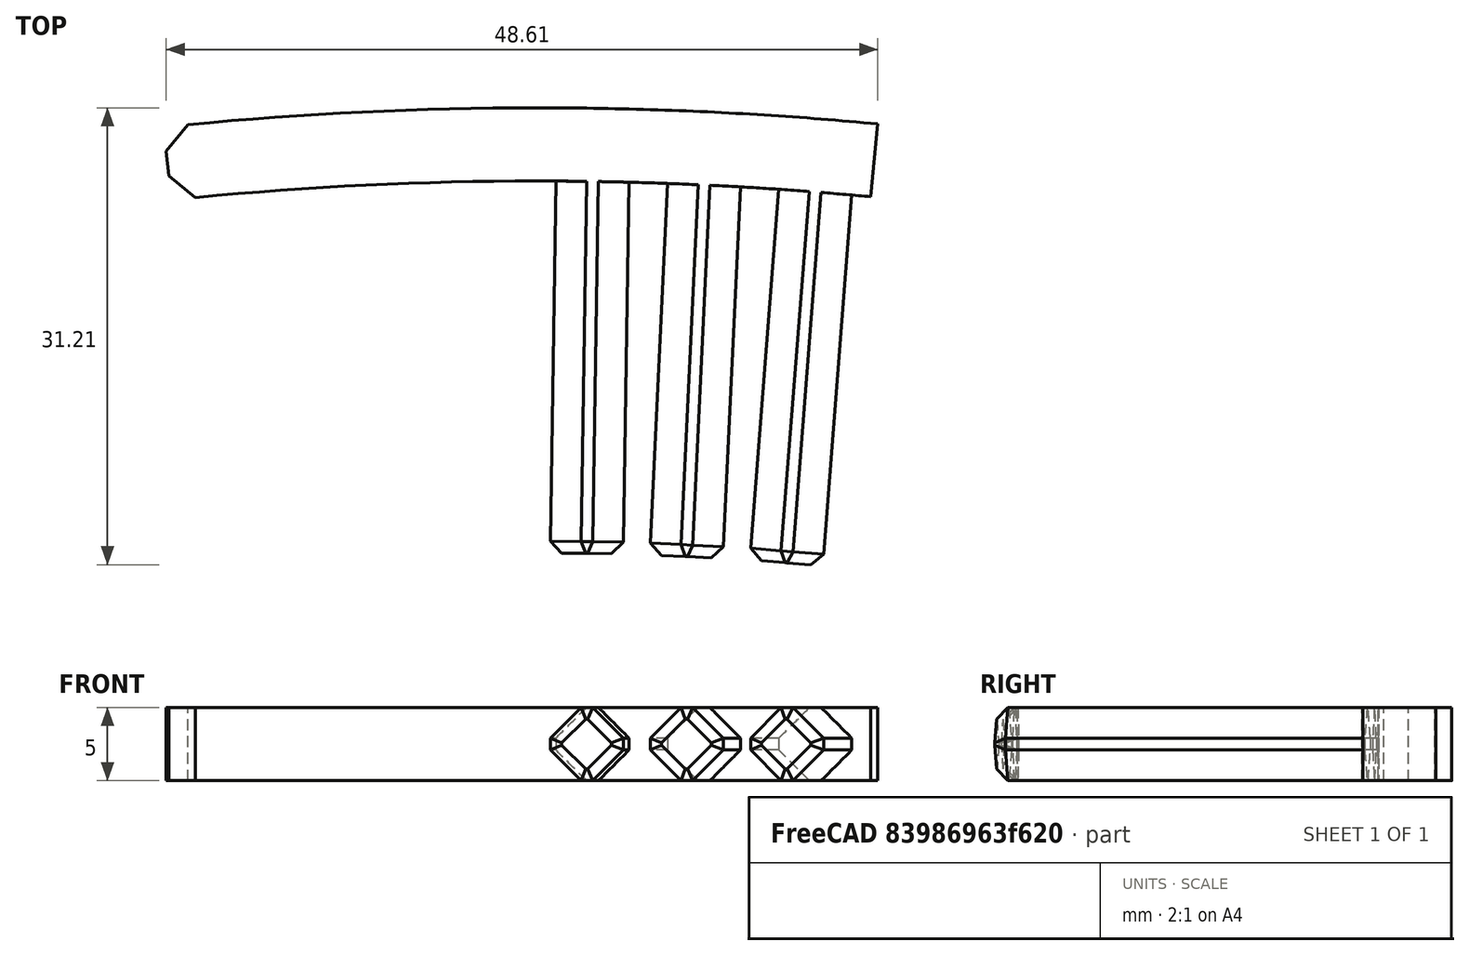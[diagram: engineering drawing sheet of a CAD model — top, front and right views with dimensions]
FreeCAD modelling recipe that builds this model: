
FCSTD DOCUMENT  (FreeCAD 1.0R39109 (Git))
Label: laser_clamp
License: All rights reserved
LicenseURL: https://en.wikipedia.org/wiki/All_rights_reserved
objects: TechDraw::DrawViewDimension×12, TechDraw::DrawProjGroupItem×4, Sketcher::SketchObject×3, PartDesign::Pad×3, PartDesign::Chamfer×2, App::VarSet×1, PartDesign::Line×1, PartDesign::Plane×1, PartDesign::PolarPattern×1, PartDesign::Body×1, App::Part×1, TechDraw::DrawSVGTemplate×1, TechDraw::DrawProjGroup×1, TechDraw::DrawViewImage×1, TechDraw::DrawPage×1
note: 47 computed .brp shape members not serialized (recipe doc carries the construction recipe); baked Part::Feature solids carry a one-line shape summary decoded from their .brp

FEATURE [App::VarSet] VarSet
  bed_adhesion_chamfer = 0.8
  bend_per_interval = 1.8
  cantilever = 25
  honeycomb_diagonal = 5.8
  interval = 7.62
  peg_length = 25.4
  pegs = 3
  real_honeycomb_radius = 1.8
  top_thickness = 5
  utility_chamfer = 1
FEATURE [Sketcher::SketchObject] Sketch
  ArcFitTolerance = 0
  AttachmentSupport = -> [XY_Plane]
  FullyConstrained = true
  MakeInternals = false
  MapMode = 5
  expr: Constraints[12] = <<VarSet>>.top_thickness
  expr: Constraints[1] = <<VarSet>>.cantilever
  expr: Constraints[21] = <<VarSet>>.interval
  expr: Constraints[25] = <<VarSet>>.bend_per_interval
  sketch-geometry (9):
    g0: LineSegment [constr] StartX=0 StartY=0 StartZ=0 EndX=-24.9668 EndY=-1.28833 EndZ=0
    g1: Circle [constr] CenterX=0 CenterY=-242.562 CenterZ=0 NormalX=0 NormalY=0 NormalZ=1 AngleXU=0 Radius=242.562
    g2: LineSegment [constr] StartX=0 StartY=0 StartZ=0 EndX=0 EndY=-242.562 EndZ=0
    g3: LineSegment StartX=-24.9668 StartY=-1.28833 StartZ=0 EndX=-25.4814 EndY=3.68511 EndZ=0
    g4: LineSegment StartX=0 StartY=0 StartZ=0 EndX=1.9e-15 EndY=5 EndZ=0
    g5: ArcOfCircle CenterX=4.17e-14 CenterY=-242.562 CenterZ=0 NormalX=0 NormalY=0 NormalZ=1 AngleXU=0 Radius=247.562 StartAngle=1.5708 EndAngle=1.67391
    g6: ArcOfCircle CenterX=2.45e-14 CenterY=-242.562 CenterZ=0 NormalX=0 NormalY=0 NormalZ=1 AngleXU=0 Radius=242.562 StartAngle=1.5708 EndAngle=1.67391
    g7: LineSegment [constr] StartX=0 StartY=0 StartZ=0 EndX=7.61906 EndY=-0.11969 EndZ=0
    g8: LineSegment [constr] StartX=7.61906 StartY=-0.11969 StartZ=0 EndX=4.17e-14 EndY=-242.562 EndZ=0
  constraints (26):
    c: Coincident(g-1,g0)
    c: Distance(g0,g0) = 25
    c: PointOnObject(g1,g-2)
    c: PointOnObject(g0,g1)
    c: PointOnObject(g0,g1)
    c: Coincident(g2,g0)
    c: Coincident(g2,g1)
    c: DistanceY(g2,g2) = 242.562  'bend_radius'
    c: Coincident(g3,g0)
    c: Coincident(g4,g0)
    c: PointOnObject(g4,g-2)
    c: Equal(g4,g3)
    c: Distance(g3,g3) = 5
    c: Perpendicular(g1,g3)
    c: Coincident(g5,g3)
    c: Coincident(g5,g4)
    c: Coincident(g6,g0)
    c: Coincident(g6,g0)
    c: Equal(g6,g1)
    c: Perpendicular(g5,g3)
    c: Coincident(g7,g0)
    c: Distance(g7,g7) = 7.62
    c: PointOnObject(g7,g1)
    c: Coincident(g8,g7)
    c: Coincident(g8,g5)
    c: Angle(g8,g2) = 0.0314159
FEATURE [PartDesign::Pad] Pad
  Direction = (0,0,1)
  Length = 5
  Length2 = 10
  Profile = -> Sketch
  ReferenceAxis = -> Sketch [N_Axis]
  Refine = true
  Suppressed = false
  Type = 0
  expr: Length = <<VarSet>>.honeycomb_diagonal - <<VarSet>>.bed_adhesion_chamfer
FEATURE [Sketcher::SketchObject] Sketch001
  ArcFitTolerance = 0
  AttachmentSupport = -> [XY_Plane]
  ExternalGeometry = -> [Pad]
  FullyConstrained = true
  MakeInternals = false
  MapMode = 5
  expr: Constraints[5] = <<VarSet>>.interval
  sketch-geometry (5):
    g0: ArcOfCircle CenterX=2.97e-14 CenterY=-242.562 CenterZ=0 NormalX=0 NormalY=0 NormalZ=1 AngleXU=0 Radius=242.562 StartAngle=1.53938 EndAngle=1.5708
    g1: ArcOfCircle CenterX=2.97e-14 CenterY=-242.562 CenterZ=0 NormalX=0 NormalY=0 NormalZ=1 AngleXU=0 Radius=247.562 StartAngle=1.53938 EndAngle=1.5708
    g2: LineSegment StartX=7.77611 StartY=4.87784 StartZ=0 EndX=7.61906 EndY=-0.11969 EndZ=0
    g3: LineSegment StartX=-9.3e-15 StartY=0 StartZ=0 EndX=-1.01e-14 EndY=5 EndZ=0
    g4: LineSegment [constr] StartX=-9.3e-15 StartY=0 StartZ=0 EndX=7.61906 EndY=-0.11969 EndZ=0
  constraints (12):
    c: Coincident(g2,g1)
    c: Coincident(g2,g0)
    c: Coincident(g3,g1)
    c: Coincident(g4,g3)
    c: Coincident(g4,g0)
    c: Distance(g4,g4) = 7.62
    c: Tangent(g0,g-1) = 1.5708
    c: Equal(g0,g-4)
    c: Perpendicular(g1,g2)
    c: Coincident(g3,g0)
    c: Coincident(g1,g-5)
    c: Coincident(g1,g0)
FEATURE [PartDesign::Line] DatumLine
  AttacherType = Attacher::AttachEngineLine
  AttachmentOffset = pos=(0,-242.562,0) rot=(0,0,1;0rad)
  AttachmentSupport = -> [Sketch001]
  Length = 20
  MapMode = 18
  Placement = pos=(0,-242.562,0) rot=(0,0,1;0rad)
  ResizeMode = 0
  expr: .AttachmentOffset.Base.y = -<<Sketch>>.Constraints.bend_radius
FEATURE [PartDesign::Pad] Pad001
  BaseFeature = -> Pad
  Direction = (0,0,1)
  Length = 5
  Length2 = 10
  Profile = -> Sketch001
  ReferenceAxis = -> Sketch001 [N_Axis]
  Refine = true
  Suppressed = false
  Type = 0
  expr: Length = Pad.Length
FEATURE [PartDesign::Plane] DatumPlane
  AttachmentOffset = pos=(0,0,0) rot=(0,0,1;4.71239rad)
  AttachmentSupport = -> [Pad001]
  Length = 60.1102
  MapMode = 45
  Placement = pos=(3.80984,-0.0398979,2.5) rot=(0.574303,-0.583396,0.574303;2.08535rad)
  ResizeMode = 0
  Width = 61.2183
FEATURE [Sketcher::SketchObject] Sketch002
  ArcFitTolerance = 0
  AttachmentOffset = pos=(0,0,0) rot=(0,0,1;4.71239rad)
  AttachmentSupport = -> [DatumPlane]
  ExternalGeometry = -> [Pad001]
  FullyConstrained = true
  MakeInternals = false
  MapMode = 5
  Placement = pos=(3.80984,-0.0398979,2.5) rot=(-0.999938,0.007854,0.007854;4.71233rad)
  expr: Constraints[24] = <<VarSet>>.bed_adhesion_chamfer
  sketch-geometry (9):
    g0: LineSegment StartX=0.4 StartY=2.5 StartZ=0 EndX=-0.4 EndY=2.5 EndZ=0
    g1: LineSegment StartX=-0.4 StartY=2.5 StartZ=0 EndX=-2.5 EndY=0.4 EndZ=0
    g2: LineSegment StartX=-2.5 StartY=0.4 StartZ=0 EndX=-2.5 EndY=-0.4 EndZ=0
    g3: LineSegment StartX=-2.5 StartY=-0.4 StartZ=0 EndX=-0.4 EndY=-2.5 EndZ=0
    g4: LineSegment StartX=-0.4 StartY=-2.5 StartZ=0 EndX=0.4 EndY=-2.5 EndZ=0
    g5: LineSegment StartX=0.4 StartY=-2.5 StartZ=0 EndX=2.5 EndY=-0.4 EndZ=0
    g6: LineSegment StartX=2.5 StartY=-0.4 StartZ=0 EndX=2.5 EndY=0.4 EndZ=0
    g7: LineSegment StartX=2.5 StartY=0.4 StartZ=0 EndX=0.4 EndY=2.5 EndZ=0
    g8: Circle [constr] CenterX=0 CenterY=0 CenterZ=0 NormalX=0 NormalY=0 NormalZ=1 AngleXU=0 Radius=2.5318
  constraints (26):
    c: Coincident(g0,g1)
    c: Coincident(g1,g2)
    c: Coincident(g2,g3)
    c: Coincident(g3,g4)
    c: Coincident(g4,g5)
    c: Coincident(g5,g6)
    c: Coincident(g6,g7)
    c: Coincident(g7,g0)
    c: PointOnObject(g0,g8)
    c: PointOnObject(g1,g8)
    c: PointOnObject(g2,g8)
    c: PointOnObject(g3,g8)
    c: PointOnObject(g4,g8)
    c: PointOnObject(g5,g8)
    c: PointOnObject(g6,g8)
    c: PointOnObject(g7,g8)
    c: Coincident(g8,g-1)
    c: Horizontal(g0)
    c: Equal(g1,g5)
    c: Equal(g5,g7)
    c: Equal(g7,g3)
    c: Equal(g0,g2)
    c: Equal(g2,g4)
    c: Equal(g4,g6)
    c: Distance(g4,g4) = 0.8
    c: PointOnObject(g4,g-4)
FEATURE [PartDesign::Pad] Pad002
  BaseFeature = -> Pad001
  Direction = (-0.0157073,-0.999877,0)
  Length = 2.5
  Length2 = 25.4
  Profile = -> Sketch002
  ReferenceAxis = -> Sketch002 [N_Axis]
  Refine = true
  Reversed = true
  Suppressed = false
  Type = 4
  expr: Length = <<VarSet>>.top_thickness / 2
  expr: Length2 = <<VarSet>>.peg_length
FEATURE [PartDesign::Chamfer] Chamfer001
  Angle = 45
  Base = -> Pad002 [Edge1,Edge2]
  BaseFeature = -> Pad002
  ChamferType = 0
  FlipDirection = false
  Refine = true
  Size = 1.66667
  Size2 = 1
  SupportTransform = false
  Suppressed = false
  UseAllEdges = false
  expr: Size = <<VarSet>>.top_thickness / 3
FEATURE [PartDesign::Chamfer] Chamfer
  Angle = 45
  Base = -> Chamfer001 [Face8]
  BaseFeature = -> Chamfer001
  ChamferType = 0
  FlipDirection = false
  Refine = true
  Size = 0.8
  Size2 = 1
  SupportTransform = false
  Suppressed = false
  UseAllEdges = false
  expr: Size = <<VarSet>>.bed_adhesion_chamfer
FEATURE [PartDesign::PolarPattern] PolarPattern
  Angle = 360
  Axis = -> DatumLine
  BaseFeature = -> Chamfer
  Mode = 1
  Occurrences = 3
  Offset = 1.8
  Originals = -> [Pad001,Pad002,Chamfer]
  Refine = true
  Reversed = true
  Suppressed = false
  TransformMode = 0
  expr: Occurrences = <<VarSet>>.pegs
  expr: Offset = <<VarSet>>.bend_per_interval
FEATURE [PartDesign::Body] Body
  AllowCompound = false
  Group = -> [Sketch,Pad,Sketch001,DatumLine,Pad001,DatumPlane,Sketch002,Pad002,Chamfer001,Chamfer,PolarPattern]
  Origin = -> Origin
  Tip = -> PolarPattern
FEATURE [App::Part] Part
  Group = -> [Body]
  Origin = -> Origin003
FEATURE [TechDraw::DrawSVGTemplate] Template
  EditableTexts = AUTHOR_NAME=Anool Mahidharia; DRAWING_TITLE=laser cutter clamp; FC-DATE=03/Jan/2025; FC-REV=REV A; FC-SC=1:1; FC-SH=1/1; FC-SI=A4; FREECAD_DRAWING=change VarSet "pegs"; Line1=Line1; Line3=to set no of pegs; PN=laser_clamp
  Height = 210
  Orientation = 1
  Template = <userpath>/Documents/FreeCAD/Templates/A4_Landscape_Wyolum.svg
  Width = 297
FEATURE [TechDraw::DrawProjGroupItem] View  label="Front"
  CoarseView = false
  Direction = (0,0,1)
  Focus = 100
  HardHidden = false
  IsoCount = 0
  IsoHidden = false
  IsoVisible = false
  LockPosition = true
  Perspective = false
  Rotation = 0
  RotationVector = (1,0,0)
  ScaleType = 2
  ScrubCount = 0
  SeamHidden = false
  SeamVisible = false
  SmoothHidden = false
  SmoothVisible = true
  Source = -> [Part]
  Type = 0
  X = 0
  XDirection = (1,0,0)
  Y = 0
FEATURE [TechDraw::DrawProjGroupItem] ProjItem  label="Bottom"
  CoarseView = false
  Direction = (0,-1,0)
  Focus = 100
  HardHidden = false
  IsoCount = 0
  IsoHidden = false
  IsoVisible = false
  LockPosition = false
  Perspective = false
  Rotation = 0
  RotationVector = (1,0,0)
  ScaleType = 0
  ScrubCount = 0
  SeamHidden = false
  SeamVisible = false
  SmoothHidden = false
  SmoothVisible = true
  Source = -> [Part]
  Type = 5
  X = 0
  XDirection = (1,0,0)
  Y = 46.9505
FEATURE [TechDraw::DrawProjGroupItem] ProjItem001  label="Left"
  CoarseView = false
  Direction = (-1,0,1e-16)
  Focus = 100
  HardHidden = false
  IsoCount = 0
  IsoHidden = false
  IsoVisible = false
  LockPosition = false
  Perspective = false
  Rotation = 0
  RotationVector = (1,0,0)
  ScaleType = 0
  ScrubCount = 0
  SeamHidden = false
  SeamVisible = false
  SmoothHidden = false
  SmoothVisible = true
  Source = -> [Part]
  Type = 1
  X = 56.6488
  XDirection = (1e-16,0,1)
  Y = 0
FEATURE [TechDraw::DrawProjGroupItem] ProjItem003  label="FrontTopLeft"
  CoarseView = false
  Direction = (-0.57735,0.57735,0.57735)
  Focus = 100
  HardHidden = false
  IsoCount = 0
  IsoHidden = false
  IsoVisible = false
  LockPosition = false
  Perspective = false
  Rotation = 0
  RotationVector = (1,0,0)
  ScaleType = 0
  ScrubCount = 0
  SeamHidden = false
  SeamVisible = false
  SmoothHidden = false
  SmoothVisible = true
  Source = -> [Part]
  Type = 6
  X = 63.7749
  XDirection = (0.707107,0,0.707107)
  Y = 61.9737
FEATURE [TechDraw::DrawProjGroup] ProjGroup
  Anchor = -> View
  AutoDistribute = false
  LockPosition = false
  ProjectionType = 1
  Rotation = 0
  ScaleType = 0
  Source = -> [Part]
  Views = -> [View,ProjItem,ProjItem001,ProjItem003]
  X = 60.4932
  Y = 96.4411
  spacingX = 15
  spacingY = 15
FEATURE [TechDraw::DrawViewDimension] Dimension
  AngleOverride = false
  Arbitrary = false
  ArbitraryTolerances = false
  BoxCorners = (2) [(-2.5,-15.6064,-1e-07),(2.5,15.6064,1e-07)]
  EqualTolerance = true
  ExtensionAngle = 0
  FormatSpec = %.2w
  FormatSpecOverTolerance = %+.2w
  FormatSpecUnderTolerance = %+.2w
  Inverted = false
  LineAngle = 0
  LockPosition = false
  MeasureType = 1
  OverTolerance = 0
  References2D = -> [ProjItem001]
  Rotation = 0
  ScaleType = 0
  TheoreticalExact = false
  Type = 1
  UnderTolerance = 0
  X = 11.3697
  Y = 22.9614
FEATURE [TechDraw::DrawViewDimension] Dimension001
  AngleOverride = false
  Arbitrary = true
  ArbitraryTolerances = false
  BoxCorners = (2) [(-24.3038,-15.6064,-1e-07),(24.3038,15.6064,1e-07)]
  EqualTolerance = true
  ExtensionAngle = 0
  FormatSpec = 25.4 mm
  FormatSpecOverTolerance = %+.2w
  FormatSpecUnderTolerance = %+.2w
  Inverted = false
  LineAngle = 0
  LockPosition = false
  MeasureType = 1
  OverTolerance = 0
  References2D = -> [View]
  Rotation = 0
  ScaleType = 0
  TheoreticalExact = false
  Type = 2
  UnderTolerance = 0
  X = -7.3651
  Y = -2.12345
FEATURE [TechDraw::DrawViewDimension] Dimension002
  AngleOverride = false
  Arbitrary = false
  ArbitraryTolerances = false
  BoxCorners = (2) [(-24.3038,-15.6064,-1e-07),(24.3038,15.6064,1e-07)]
  EqualTolerance = true
  ExtensionAngle = 0
  FormatSpec = %.2w
  FormatSpecOverTolerance = %+.2w
  FormatSpecUnderTolerance = %+.2w
  Inverted = false
  LineAngle = 0
  LockPosition = false
  MeasureType = 1
  OverTolerance = 0
  References2D = -> [View]
  Rotation = 0
  ScaleType = 0
  TheoreticalExact = false
  Type = 0
  UnderTolerance = 0
  X = 32.9506
  Y = 20.9358
FEATURE [TechDraw::DrawViewDimension] Dimension003
  AngleOverride = false
  Arbitrary = false
  ArbitraryTolerances = false
  BoxCorners = (2) [(-24.3038,-15.6064,-1e-07),(24.3038,15.6064,1e-07)]
  EqualTolerance = true
  ExtensionAngle = 0
  FormatSpec = %.2w
  FormatSpecOverTolerance = %+.2w
  FormatSpecUnderTolerance = %+.2w
  Inverted = false
  LineAngle = 0
  LockPosition = false
  MeasureType = 1
  OverTolerance = 0
  References2D = -> [View]
  Rotation = 0
  ScaleType = 0
  TheoreticalExact = false
  Type = 1
  UnderTolerance = 0
  X = 0.743417
  Y = 21.8989
FEATURE [TechDraw::DrawViewDimension] Dimension004
  AngleOverride = false
  Arbitrary = false
  ArbitraryTolerances = false
  BoxCorners = (2) [(-24.3038,-15.6064,-1e-07),(24.3038,15.6064,1e-07)]
  EqualTolerance = true
  ExtensionAngle = 0
  FormatSpec = R%.2w
  FormatSpecOverTolerance = %+.2w
  FormatSpecUnderTolerance = %+.2w
  Inverted = false
  LineAngle = 0
  LockPosition = false
  MeasureType = 1
  OverTolerance = 0
  References2D = -> [View]
  Rotation = 0
  ScaleType = 0
  TheoreticalExact = false
  Type = 4
  UnderTolerance = 0
  X = -15.8478
  Y = -3.8872
FEATURE [TechDraw::DrawViewDimension] Dimension005
  AngleOverride = false
  Arbitrary = false
  ArbitraryTolerances = false
  BoxCorners = (2) [(-24.3038,-2.5,-1e-07),(24.3038,2.5,1e-07)]
  EqualTolerance = true
  ExtensionAngle = 0
  FormatSpec = %.2w
  FormatSpecOverTolerance = %+.2w
  FormatSpecUnderTolerance = %+.2w
  Inverted = false
  LineAngle = 0
  LockPosition = false
  MeasureType = 1
  OverTolerance = 0
  References2D = -> [ProjItem]
  Rotation = 0
  ScaleType = 0
  TheoreticalExact = false
  Type = 2
  UnderTolerance = 0
  X = 28.1101
  Y = 11.9524
FEATURE [TechDraw::DrawViewDimension] Dimension006
  AngleOverride = false
  Arbitrary = false
  ArbitraryTolerances = false
  BoxCorners = (2) [(-24.3038,-2.5,-1e-07),(24.3038,2.5,1e-07)]
  EqualTolerance = true
  ExtensionAngle = 0
  FormatSpec = %.2w
  FormatSpecOverTolerance = %+.2w
  FormatSpecUnderTolerance = %+.2w
  Inverted = false
  LineAngle = 0
  LockPosition = false
  MeasureType = 1
  OverTolerance = 0
  References2D = -> [ProjItem]
  Rotation = 0
  ScaleType = 0
  TheoreticalExact = false
  Type = 1
  UnderTolerance = 0
  X = -6.34307
  Y = 17.5518
FEATURE [TechDraw::DrawViewDimension] Dimension007
  AngleOverride = false
  Arbitrary = false
  ArbitraryTolerances = false
  BoxCorners = (2) [(-2.5,-15.6064,-1e-07),(2.5,15.6064,1e-07)]
  EqualTolerance = true
  ExtensionAngle = 0
  FormatSpec = %.2w
  FormatSpecOverTolerance = %+.2w
  FormatSpecUnderTolerance = %+.2w
  Inverted = false
  LineAngle = 0
  LockPosition = false
  MeasureType = 1
  OverTolerance = 0
  References2D = -> [ProjItem001]
  Rotation = 0
  ScaleType = 0
  TheoreticalExact = false
  Type = 1
  UnderTolerance = 0
  X = 14.377
  Y = -17.2221
FEATURE [TechDraw::DrawViewDimension] Dimension008
  AngleOverride = false
  Arbitrary = false
  ArbitraryTolerances = false
  BoxCorners = (2) [(-24.3038,-2.5,-1e-07),(24.3038,2.5,1e-07)]
  EqualTolerance = true
  ExtensionAngle = 0
  FormatSpec = %.2w
  FormatSpecOverTolerance = %+.2w
  FormatSpecUnderTolerance = %+.2w
  Inverted = false
  LineAngle = 0
  LockPosition = false
  MeasureType = 1
  OverTolerance = 0
  References2D = -> [ProjItem]
  Rotation = 0
  ScaleType = 0
  TheoreticalExact = false
  Type = 1
  UnderTolerance = 0
  X = -11.6488
  Y = 8.9614
FEATURE [TechDraw::DrawViewDimension] Dimension009
  AngleOverride = false
  Arbitrary = false
  ArbitraryTolerances = false
  BoxCorners = (2) [(-24.3038,-15.6064,-1e-07),(24.3038,15.6064,1e-07)]
  EqualTolerance = true
  ExtensionAngle = 0
  FormatSpec = %.2w
  FormatSpecOverTolerance = %+.2w
  FormatSpecUnderTolerance = %+.2w
  Inverted = false
  LineAngle = 0
  LockPosition = false
  MeasureType = 1
  OverTolerance = 0
  References2D = -> [View]
  Rotation = 0
  ScaleType = 0
  TheoreticalExact = false
  Type = 6
  UnderTolerance = 0
  X = -1.48243
  Y = 29.4255
FEATURE [TechDraw::DrawViewDimension] Dimension010
  AngleOverride = false
  Arbitrary = false
  ArbitraryTolerances = false
  BoxCorners = (2) [(-24.3038,-15.6064,-1e-07),(24.3038,15.6064,1e-07)]
  EqualTolerance = true
  ExtensionAngle = 0
  FormatSpec = %.2w
  FormatSpecOverTolerance = %+.2w
  FormatSpecUnderTolerance = %+.2w
  Inverted = false
  LineAngle = 0
  LockPosition = false
  MeasureType = 1
  OverTolerance = 0
  References2D = -> [View]
  Rotation = 0
  ScaleType = 0
  TheoreticalExact = false
  Type = 6
  UnderTolerance = 0
  X = 2.21075
  Y = -18.8169
FEATURE [TechDraw::DrawViewDimension] Dimension011
  AngleOverride = false
  Arbitrary = false
  ArbitraryTolerances = false
  BoxCorners = (2) [(-24.3038,-15.6064,-1e-07),(24.3038,15.6064,1e-07)]
  EqualTolerance = true
  ExtensionAngle = 0
  FormatSpec = %.2w
  FormatSpecOverTolerance = %+.2w
  FormatSpecUnderTolerance = %+.2w
  Inverted = false
  LineAngle = 0
  LockPosition = false
  MeasureType = 1
  OverTolerance = 0
  References2D = -> [View]
  Rotation = 0
  ScaleType = 0
  TheoreticalExact = false
  Type = 6
  UnderTolerance = 0
  X = 20.8461
  Y = -19.8022
FEATURE [TechDraw::DrawViewImage] ActiveView
  Height = 102.4
  ImageFile = <userpath>/.cache/FreeCAD/Cache/FreeCAD_Doc_609d2900-1335-4912-bd14-662a7bb4634d_ceccc3_761232/PageActiveViewhaZNJK.png
  LockPosition = false
  Rotation = 0
  ScaleType = 2
  Width = 128
  X = 220.733
  Y = 118.291
FEATURE [TechDraw::DrawPage] Page
  KeepUpdated = true
  NextBalloonIndex = 1
  ProjectionType = 0
  Template = -> Template
  Views = -> [ProjGroup,Dimension,Dimension001,Dimension002,Dimension003,Dimension004,Dimension005,Dimension006,Dimension007,Dimension008,Dimension009,Dimension010,Dimension011,ActiveView]
